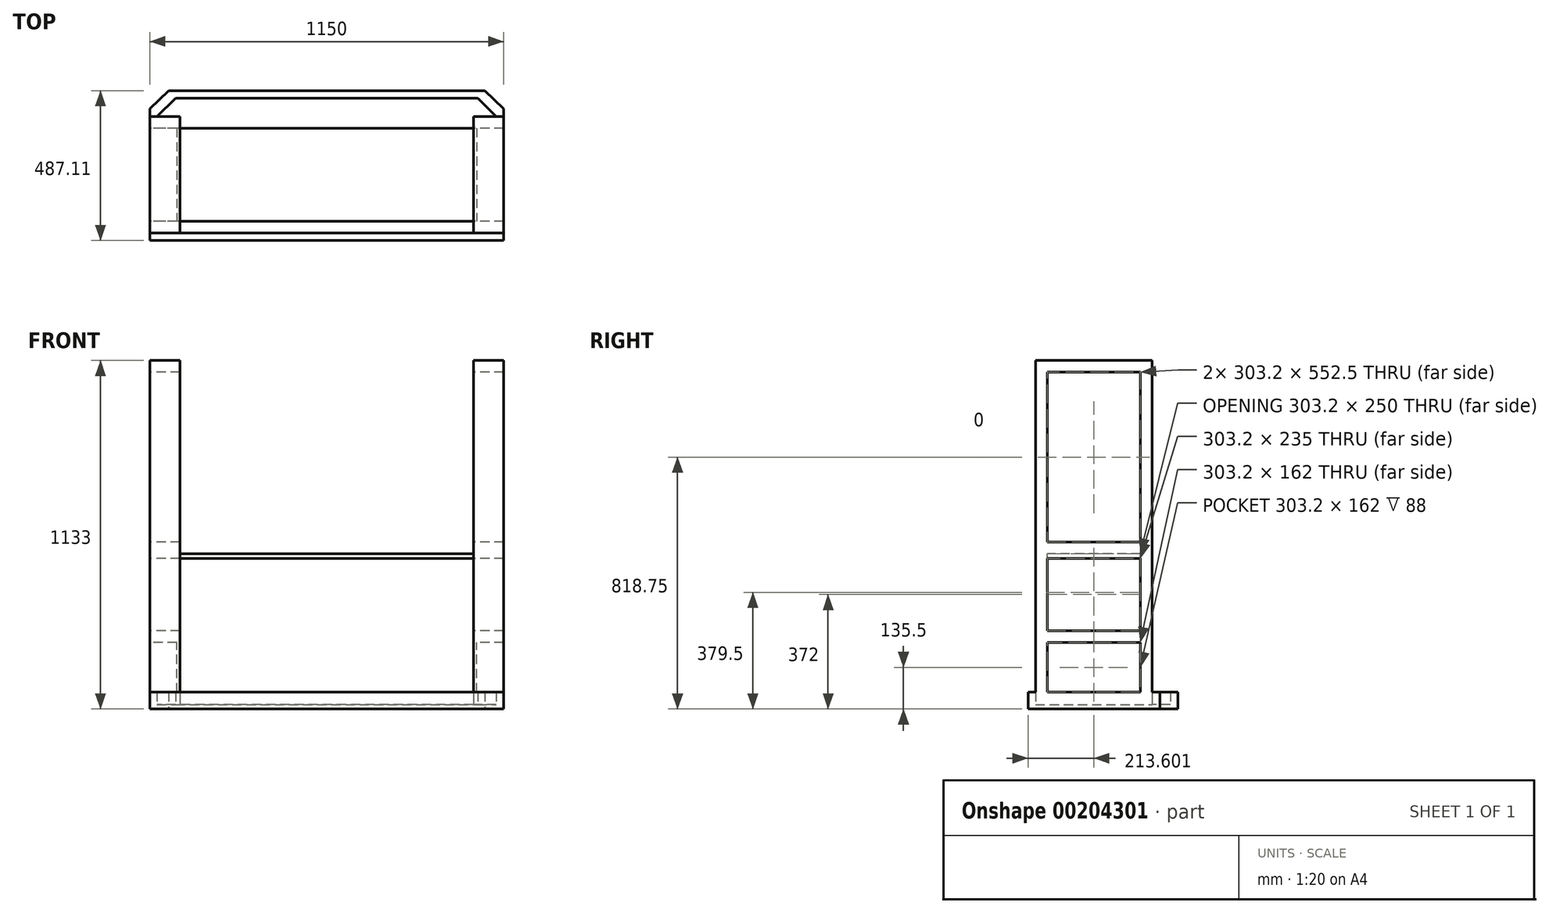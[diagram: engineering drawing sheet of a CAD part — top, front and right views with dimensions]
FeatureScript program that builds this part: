
annotation { "Feature Type Name" : "Feature", "Feature Type Description" : "" }
export const myFeature = defineFeature(function(context is Context, id is Id, definition is map)
    precondition{}
    {
        {
            var Q0;
            Q0=qCreatedBy(makeId("Top.planeOp"),FACE);
            var sketch = newSketch(context, id + "F0", { "sketchPlane" : qUnion([Q0])});
            skLineSegment(sketch, "E0", {"start": v(-575.48, -331.45) * mm, "end": v(574.52, -331.45) * mm});
            skLineSegment(sketch, "E1", {"start": v(-575.48, -331.45) * mm, "end": v(-575.48, 96.55) * mm});
            skLineSegment(sketch, "E2", {"start": v(-575.48, 96.55) * mm, "end": v(-514.4, 155.66) * mm});
            skLineSegment(sketch, "E3", {"start": v(-514.4, 155.66) * mm, "end": v(513.44, 155.66) * mm});
            skLineSegment(sketch, "E4", {"start": v(513.44, 155.66) * mm, "end": v(574.52, 96.55) * mm});
            skLineSegment(sketch, "E5", {"start": v(574.52, 96.55) * mm, "end": v(574.52, -331.45) * mm});
            skLineSegment(sketch, "E6", {"start": v(-551.48, -307.45) * mm, "end": v(550.52, -307.45) * mm});
            skLineSegment(sketch, "E7", {"start": v(550.52, -307.45) * mm, "end": v(550.52, 71.75) * mm});
            skLineSegment(sketch, "E8", {"start": v(550.52, 71.75) * mm, "end": v(490.2, 131.66) * mm});
            skLineSegment(sketch, "E9", {"start": v(490.2, 131.66) * mm, "end": v(-491.18, 131.66) * mm});
            skLineSegment(sketch, "E10", {"start": v(-551.48, -307.45) * mm, "end": v(-551.48, 71.75) * mm});
            skLineSegment(sketch, "E11", {"start": v(-551.48, 71.75) * mm, "end": v(-491.18, 131.66) * mm});
            skLineSegment(sketch, "E12", {"start": v(-575.48, 96.55) * mm, "end": v(-551.48, 71.75) * mm});
            skLineSegment(sketch, "E13", {"start": v(-514.4, 155.66) * mm, "end": v(-491.18, 131.66) * mm});
            skLineSegment(sketch, "E14", {"start": v(-575.48, -331.45) * mm, "end": v(-551.48, -307.45) * mm});
            skLineSegment(sketch, "E15", {"start": v(574.52, -331.45) * mm, "end": v(550.52, -307.45) * mm});
            skLineSegment(sketch, "E16", {"start": v(550.52, 71.75) * mm, "end": v(574.52, 96.55) * mm});
            skLineSegment(sketch, "E17", {"start": v(490.2, 131.66) * mm, "end": v(513.44, 155.66) * mm});
            skSolve(sketch);
        }
        {
            var Q0;
            Q0=makeQuery(id+"F0.imprint","IMPRINT",FACE,{"disambiguationData":[TD([[makeQuery(id+"F0.imprint","IMPRINT",EDGE,{"derivedFrom":sQuery(id+"F0.wireOp",EDGE,"E4")}),-1.0]])]});
            var Q1;
            Q1=makeQuery(id+"F0.imprint","IMPRINT",FACE,{"disambiguationData":[TD([[makeQuery(id+"F0.imprint","IMPRINT",EDGE,{"derivedFrom":sQuery(id+"F0.wireOp",EDGE,"E3")}),-1.0]])]});
            var Q2;
            Q2=makeQuery(id+"F0.imprint","IMPRINT",FACE,{"disambiguationData":[TD([[makeQuery(id+"F0.imprint","IMPRINT",EDGE,{"derivedFrom":sQuery(id+"F0.wireOp",EDGE,"E2")}),-1.0]])]});
            var Q3;
            Q3=makeQuery(id+"F0.imprint","IMPRINT",FACE,{"disambiguationData":[TD([[makeQuery(id+"F0.imprint","IMPRINT",EDGE,{"derivedFrom":sQuery(id+"F0.wireOp",EDGE,"E1")}),-1.0]])]});
            var Q4;
            Q4=makeQuery(id+"F0.imprint","IMPRINT",FACE,{"disambiguationData":[TD([[makeQuery(id+"F0.imprint","IMPRINT",EDGE,{"derivedFrom":sQuery(id+"F0.wireOp",EDGE,"E5")}),-1.0]])]});
            var Q5;
            Q5=makeQuery(id+"F0.imprint","IMPRINT",FACE,{"disambiguationData":[TD([[makeQuery(id+"F0.imprint","IMPRINT",EDGE,{"derivedFrom":sQuery(id+"F0.wireOp",EDGE,"E0")}),1.0]])]});
            var Q6;
            Q6=makeQuery(id+"F0.imprint","IMPRINT",FACE,{"disambiguationData":[TD([[makeQuery(id+"F0.imprint","IMPRINT",EDGE,{"derivedFrom":sQuery(id+"F0.wireOp",EDGE,"E6")}),1.0]])]});
            extrude(context, id + "F1", {"entities" : qUnion([Q0, Q1, Q2, Q3, Q4, Q5, Q6]), "endBound" : BoundingType.SYMMETRIC, "depth" : 15 * mm});
        }
        {
            var Q0;
            Q0 = qSketchRegion(id + "F0", true);
            extrude(context, id + "F2", {"entities" : qUnion([Q0]), "operationType" : NewBodyOperationType.ADD, "depth" : 47 * mm});
        }
        {
            var Q0;
            Q0=makeQuery(id+"F1.opExtrude","CAP_FACE",FACE,{"disambiguationData":[OSD([sQuery(id+"F0.wireOp",EDGE,"E0"),sQuery(id+"F0.wireOp",EDGE,"E1"),sQuery(id+"F0.wireOp",EDGE,"E2"),sQuery(id+"F0.wireOp",EDGE,"E3"),sQuery(id+"F0.wireOp",EDGE,"E4"),sQuery(id+"F0.wireOp",EDGE,"E5")])],"isStart":false});
            var sketch = newSketch(context, id + "F3", { "sketchPlane" : qUnion([Q0])});
            skLineSegment(sketch, "E18.bottom", {"start": v(-575.48, -307.45) * mm, "end": v(-477.48, -307.45) * mm});
            skLineSegment(sketch, "E18.top", {"start": v(-575.48, -269.45) * mm, "end": v(-477.48, -269.45) * mm});
            skLineSegment(sketch, "E18.left", {"start": v(-575.48, -307.45) * mm, "end": v(-575.48, -269.45) * mm});
            skLineSegment(sketch, "E18.right", {"start": v(-477.48, -307.45) * mm, "end": v(-477.48, -269.45) * mm});
            skLineSegment(sketch, "E19.bottom", {"start": v(574.52, -307.45) * mm, "end": v(476.52, -307.45) * mm});
            skLineSegment(sketch, "E19.top", {"start": v(574.52, -269.45) * mm, "end": v(476.52, -269.45) * mm});
            skLineSegment(sketch, "E19.left", {"start": v(574.52, -307.45) * mm, "end": v(574.52, -269.45) * mm});
            skLineSegment(sketch, "E19.right", {"start": v(476.52, -307.45) * mm, "end": v(476.52, -269.45) * mm});
            skLineSegment(sketch, "E20.bottom", {"start": v(-575.48, 71.75) * mm, "end": v(-477.48, 71.75) * mm});
            skLineSegment(sketch, "E20.top", {"start": v(-575.48, 33.75) * mm, "end": v(-477.48, 33.75) * mm});
            skLineSegment(sketch, "E20.left", {"start": v(-575.48, 71.75) * mm, "end": v(-575.48, 33.75) * mm});
            skLineSegment(sketch, "E20.right", {"start": v(-477.48, 71.75) * mm, "end": v(-477.48, 33.75) * mm});
            skLineSegment(sketch, "E21.bottom", {"start": v(574.52, 71.75) * mm, "end": v(476.52, 71.75) * mm});
            skLineSegment(sketch, "E21.top", {"start": v(574.52, 33.75) * mm, "end": v(476.52, 33.75) * mm});
            skLineSegment(sketch, "E21.left", {"start": v(574.52, 71.75) * mm, "end": v(574.52, 33.75) * mm});
            skLineSegment(sketch, "E21.right", {"start": v(476.52, 71.75) * mm, "end": v(476.52, 33.75) * mm});
            skLineSegment(sketch, "E22.left", {"start": v(-575.48, 33.75) * mm, "end": v(-575.48, -269.45) * mm});
            skLineSegment(sketch, "E22.right", {"start": v(-477.48, 33.75) * mm, "end": v(-477.48, -269.45) * mm});
            skLineSegment(sketch, "E23.bottom", {"start": v(476.52, 33.75) * mm, "end": v(574.52, 33.75) * mm});
            skLineSegment(sketch, "E23.top", {"start": v(476.52, -269.45) * mm, "end": v(574.52, -269.45) * mm});
            skLineSegment(sketch, "E23.left", {"start": v(476.52, 33.75) * mm, "end": v(476.52, -269.45) * mm});
            skLineSegment(sketch, "E23.right", {"start": v(574.52, 33.75) * mm, "end": v(574.52, -269.45) * mm});
            skSolve(sketch);
        }
        {
            var Q0;
            Q0 = qSketchRegion(id + "F3", true);
            extrude(context, id + "F4", {"entities" : qUnion([Q0]), "operationType" : NewBodyOperationType.ADD, "depth" : 1080 * mm});
        }
        {
            var Q0;
            {var subQ0=sQuery(id+"F0.wireOp",EDGE,"E1");Q0=makeQuery(id+"F4.boolean.opBoolean","MERGE",FACE,{"derivedFrom":[makeQuery(id+"F2.boolean.opBoolean","MERGE",FACE,{"derivedFrom":[makeQuery(id+"F1.opExtrude","SWEPT_FACE",FACE,{"disambiguationData":[OSD([subQ0])]}),makeQuery(id+"F2.opExtrude","SWEPT_FACE",FACE,{"disambiguationData":[OSD([subQ0])]})]}),makeQuery(id+"F4.opExtrude","SWEPT_FACE",FACE,{"disambiguationData":[OSD([sQuery(id+"F3.wireOp",EDGE,"E18.left"),sQuery(id+"F3.wireOp",EDGE,"E20.left"),sQuery(id+"F3.wireOp",EDGE,"E22.left")])]})]});}
            var sketch = newSketch(context, id + "F5", { "sketchPlane" : qUnion([Q0])});
            skLineSegment(sketch, "E24.bottom", {"start": v(-33.75, 247) * mm, "end": v(269.45, 247) * mm});
            skLineSegment(sketch, "E24.top", {"start": v(-33.75, 497) * mm, "end": v(269.45, 497) * mm});
            skLineSegment(sketch, "E24.left", {"start": v(-33.75, 247) * mm, "end": v(-33.75, 497) * mm});
            skLineSegment(sketch, "E24.right", {"start": v(269.45, 247) * mm, "end": v(269.45, 497) * mm});
            skLineSegment(sketch, "E25.bottom", {"start": v(-33.75, 535) * mm, "end": v(269.45, 535) * mm});
            skLineSegment(sketch, "E25.top", {"start": v(-33.75, 1087.5) * mm, "end": v(269.45, 1087.5) * mm});
            skLineSegment(sketch, "E25.left", {"start": v(-33.75, 535) * mm, "end": v(-33.75, 1087.5) * mm});
            skLineSegment(sketch, "E25.right", {"start": v(269.45, 535) * mm, "end": v(269.45, 1087.5) * mm});
            skLineSegment(sketch, "E26.bottom", {"start": v(-71.75, 1087.5) * mm, "end": v(307.45, 1087.5) * mm});
            skLineSegment(sketch, "E26.top", {"start": v(-71.75, 1125.5) * mm, "end": v(307.45, 1125.5) * mm});
            skLineSegment(sketch, "E26.left", {"start": v(-71.75, 1087.5) * mm, "end": v(-71.75, 1125.5) * mm});
            skLineSegment(sketch, "E26.right", {"start": v(307.45, 1087.5) * mm, "end": v(307.45, 1125.5) * mm});
            skLineSegment(sketch, "E27.bottom", {"start": v(-33.75, 47) * mm, "end": v(269.45, 47) * mm});
            skLineSegment(sketch, "E27.top", {"start": v(-33.75, 209) * mm, "end": v(269.45, 209) * mm});
            skLineSegment(sketch, "E27.left", {"start": v(-33.75, 47) * mm, "end": v(-33.75, 209) * mm});
            skLineSegment(sketch, "E27.right", {"start": v(269.45, 47) * mm, "end": v(269.45, 209) * mm});
            skLineSegment(sketch, "E28.top", {"start": v(-33.75, 482) * mm, "end": v(269.45, 482) * mm});
            skLineSegment(sketch, "E28.left", {"start": v(-33.75, 497) * mm, "end": v(-33.75, 482) * mm});
            skLineSegment(sketch, "E28.right", {"start": v(269.45, 497) * mm, "end": v(269.45, 482) * mm});
            skSolve(sketch);
        }
        {
            var Q0;
            Q0=makeQuery(id+"F5.imprint","IMPRINT",FACE,{"disambiguationData":[TD([[makeQuery(id+"F5.imprint","IMPRINT",EDGE,{"derivedFrom":sQuery(id+"F5.wireOp",EDGE,"E25.bottom")}),1.0]])]});
            var Q1;
            Q1=makeQuery(id+"F5.imprint","IMPRINT",FACE,{"disambiguationData":[TD([[makeQuery(id+"F5.imprint","IMPRINT",EDGE,{"derivedFrom":sQuery(id+"F5.wireOp",EDGE,"E24.bottom")}),1.0]])]});
            extrude(context, id + "F6", {"entities" : qUnion([Q0, Q1]), "operationType" : NewBodyOperationType.REMOVE, "endBound" : BoundingType.THROUGH_ALL, "oppositeDirection" : true, "depth" : 25 * mm});
        }
        {
            var Q0;
            Q0=makeQuery(id+"F5.imprint","IMPRINT",FACE,{"disambiguationData":[TD([[makeQuery(id+"F5.imprint","IMPRINT",EDGE,{"derivedFrom":sQuery(id+"F5.wireOp",EDGE,"E26.top")}),-1.0]])]});
            extrude(context, id + "F7", {"entities" : qUnion([Q0]), "operationType" : NewBodyOperationType.ADD, "oppositeDirection" : true, "depth" : 1150 * mm});
        }
        {
            var Q0;
            Q0=makeQuery(id+"F7.opExtrude","SWEPT_FACE",FACE,{"disambiguationData":[OSD([sQuery(id+"F5.wireOp",EDGE,"E26.top")])]});
            var sketch = newSketch(context, id + "F8", { "sketchPlane" : qUnion([Q0])});
            skLineSegment(sketch, "E29.bottom", {"start": v(-477.48, 71.75) * mm, "end": v(476.52, 71.75) * mm});
            skLineSegment(sketch, "E29.top", {"start": v(-477.48, -307.45) * mm, "end": v(476.52, -307.45) * mm});
            skLineSegment(sketch, "E29.left", {"start": v(-477.48, 71.75) * mm, "end": v(-477.48, -307.45) * mm});
            skLineSegment(sketch, "E29.right", {"start": v(476.52, 71.75) * mm, "end": v(476.52, -307.45) * mm});
            skSolve(sketch);
        }
        {
            var Q0;
            Q0=makeQuery(id+"F8.imprint","IMPRINT",FACE,{"disambiguationData":[TD([[makeQuery(id+"F8.imprint","IMPRINT",EDGE,{"derivedFrom":sQuery(id+"F8.wireOp",EDGE,"E29.bottom")}),1.0]])]});
            extrude(context, id + "F9", {"entities" : qUnion([Q0]), "operationType" : NewBodyOperationType.REMOVE, "endBound" : BoundingType.SYMMETRIC, "oppositeDirection" : true, "depth" : 98 * mm});
        }
        {
            var Q0;
            Q0=makeQuery(id+"F5.imprint","IMPRINT",FACE,{"disambiguationData":[TD([[makeQuery(id+"F5.imprint","IMPRINT",EDGE,{"derivedFrom":sQuery(id+"F5.wireOp",EDGE,"E27.bottom")}),1.0]])]});
            extrude(context, id + "F10", {"entities" : qUnion([Q0]), "operationType" : NewBodyOperationType.REMOVE, "oppositeDirection" : true, "depth" : 1150 * mm});
        }
        {
            var Q0;
            Q0=makeQuery(id+"F9.boolean.opBoolean","MERGE",FACE,{"derivedFrom":[makeQuery(id+"F4.opExtrude","SWEPT_FACE",FACE,{"disambiguationData":[OSD([sQuery(id+"F3.wireOp",EDGE,"E18.right"),sQuery(id+"F3.wireOp",EDGE,"E20.right"),sQuery(id+"F3.wireOp",EDGE,"E22.right")])]}),makeQuery(id+"F9.opExtrude","SWEPT_FACE",FACE,{"disambiguationData":[OSD([sQuery(id+"F8.wireOp",EDGE,"E29.left")])]})]});
            var sketch = newSketch(context, id + "F11", { "sketchPlane" : qUnion([Q0])});
            skLineSegment(sketch, "E30.bottom", {"start": v(-269.45, 209) * mm, "end": v(33.75, 209) * mm});
            skLineSegment(sketch, "E30.top", {"start": v(-269.45, 47) * mm, "end": v(33.75, 47) * mm});
            skLineSegment(sketch, "E30.left", {"start": v(-269.45, 209) * mm, "end": v(-269.45, 47) * mm});
            skLineSegment(sketch, "E30.right", {"start": v(33.75, 209) * mm, "end": v(33.75, 47) * mm});
            skSolve(sketch);
        }
        {
            var Q0;
            Q0=makeQuery(id+"F11.imprint","IMPRINT",FACE,{"disambiguationData":[TD([[makeQuery(id+"F11.imprint","IMPRINT",EDGE,{"derivedFrom":sQuery(id+"F11.wireOp",EDGE,"E30.bottom")}),1.0]])]});
            extrude(context, id + "F12", {"entities" : qUnion([Q0]), "operationType" : NewBodyOperationType.ADD, "oppositeDirection" : true, "depth" : 10 * mm});
        }
        {
            var Q0;
            Q0=makeQuery(id+"F9.boolean.opBoolean","MERGE",FACE,{"derivedFrom":[makeQuery(id+"F4.opExtrude","SWEPT_FACE",FACE,{"disambiguationData":[OSD([sQuery(id+"F3.wireOp",EDGE,"E19.right"),sQuery(id+"F3.wireOp",EDGE,"E21.right"),sQuery(id+"F3.wireOp",EDGE,"E23.left")])]}),makeQuery(id+"F9.opExtrude","SWEPT_FACE",FACE,{"disambiguationData":[OSD([sQuery(id+"F8.wireOp",EDGE,"E29.right")])]})]});
            var sketch = newSketch(context, id + "F13", { "sketchPlane" : qUnion([Q0])});
            skLineSegment(sketch, "E31.bottom", {"start": v(-33.75, 209) * mm, "end": v(269.45, 209) * mm});
            skLineSegment(sketch, "E31.top", {"start": v(-33.75, 47) * mm, "end": v(269.45, 47) * mm});
            skLineSegment(sketch, "E31.left", {"start": v(-33.75, 209) * mm, "end": v(-33.75, 47) * mm});
            skLineSegment(sketch, "E31.right", {"start": v(269.45, 209) * mm, "end": v(269.45, 47) * mm});
            skSolve(sketch);
        }
        {
            var Q0;
            Q0=makeQuery(id+"F13.imprint","IMPRINT",FACE,{"disambiguationData":[TD([[makeQuery(id+"F13.imprint","IMPRINT",EDGE,{"derivedFrom":sQuery(id+"F13.wireOp",EDGE,"E31.bottom")}),-1.0]])]});
            extrude(context, id + "F14", {"entities" : qUnion([Q0]), "operationType" : NewBodyOperationType.ADD, "oppositeDirection" : true, "depth" : 10 * mm});
        }
        {
            var Q0;
            Q0=makeQuery(id+"F5.imprint","IMPRINT",FACE,{"disambiguationData":[TD([[makeQuery(id+"F5.imprint","IMPRINT",EDGE,{"derivedFrom":sQuery(id+"F5.wireOp",EDGE,"E24.top")}),-1.0]])]});
            extrude(context, id + "F15", {"entities" : qUnion([Q0]), "operationType" : NewBodyOperationType.ADD, "oppositeDirection" : true, "depth" : 1150 * mm});
        }
    });
